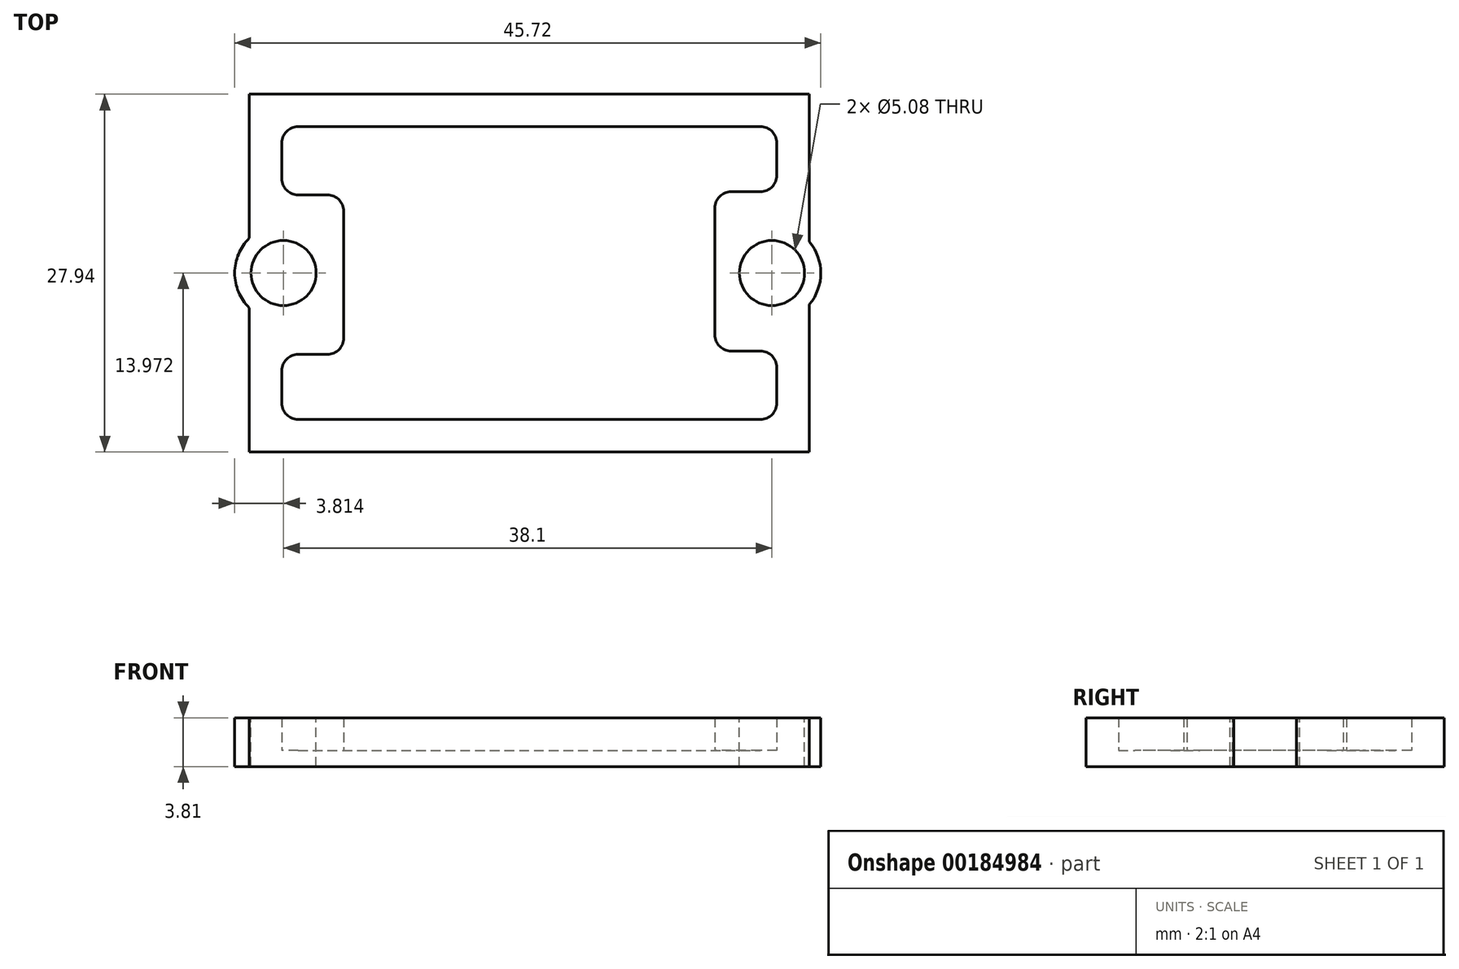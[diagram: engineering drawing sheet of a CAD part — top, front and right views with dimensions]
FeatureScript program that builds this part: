
annotation { "Feature Type Name" : "Feature", "Feature Type Description" : "" }
export const myFeature = defineFeature(function(context is Context, id is Id, definition is map)
    precondition{}
    {
        {
            var Q0;
            Q0=qCreatedBy(makeId("Top.planeOp"),FACE);
            var sketch = newSketch(context, id + "F0", { "sketchPlane" : qUnion([Q0])});
            skLineSegment(sketch, "E0.bottom", {"start": v(-19.02, 13.8) * mm, "end": v(17.05, 13.8) * mm});
            skLineSegment(sketch, "E0.top", {"start": v(-19.02, -9.06) * mm, "end": v(17.05, -9.06) * mm});
            skLineSegment(sketch, "E0.left", {"start": v(-20.3, -5.25) * mm, "end": v(-20.3, -7.79) * mm});
            skLineSegment(sketch, "E0.right", {"start": v(18.32, 12.53) * mm, "end": v(18.32, 10) * mm});
            skLineSegment(sketch, "E1.bottom", {"start": v(-19.02, 8.47) * mm, "end": v(-16.74, 8.47) * mm});
            skLineSegment(sketch, "E1.top", {"start": v(-19.02, -3.98) * mm, "end": v(-16.74, -3.98) * mm});
            skLineSegment(sketch, "E1.right", {"start": v(-15.47, 7.2) * mm, "end": v(-15.47, -2.7) * mm});
            skLineSegment(sketch, "E2.bottom", {"start": v(17.05, 8.72) * mm, "end": v(14.76, 8.72) * mm});
            skLineSegment(sketch, "E2.top", {"start": v(17.05, -3.72) * mm, "end": v(14.76, -3.72) * mm});
            skLineSegment(sketch, "E2.right", {"start": v(13.49, 7.45) * mm, "end": v(13.49, -2.45) * mm});
            skPoint(sketch, "E3.visualSharp", {"position": v(-15.47, 8.47) * mm});
            skArc(sketch, "E3.filletArc", {"start": v(-15.47, 7.2) * mm, "mid": v(-15.84, 8.1) * mm, "end": v(-16.74, 8.47) * mm});
            skPoint(sketch, "E4.visualSharp", {"position": v(-15.47, -3.98) * mm});
            skArc(sketch, "E4.filletArc", {"start": v(-16.74, -3.98) * mm, "mid": v(-15.84, -3.6) * mm, "end": v(-15.47, -2.7) * mm});
            skArc(sketch, "E5.filletArc", {"start": v(-19.02, -3.98) * mm, "mid": v(-19.92, -4.35) * mm, "end": v(-20.3, -5.25) * mm});
            skPoint(sketch, "E6.visualSharp", {"position": v(-20.3, -9.06) * mm});
            skArc(sketch, "E6.filletArc", {"start": v(-20.3, -7.79) * mm, "mid": v(-19.92, -8.69) * mm, "end": v(-19.02, -9.06) * mm});
            skLineSegment(sketch, "E7", {"start": v(-20.3, 9.74) * mm, "end": v(-20.3, 12.53) * mm});
            skPoint(sketch, "E8.visualSharp", {"position": v(-20.3, 13.8) * mm});
            skArc(sketch, "E8.filletArc", {"start": v(-19.02, 13.8) * mm, "mid": v(-19.92, 13.43) * mm, "end": v(-20.3, 12.53) * mm});
            skPoint(sketch, "E9.visualSharp", {"position": v(-20.3, 8.47) * mm});
            skArc(sketch, "E9.filletArc", {"start": v(-20.3, 9.74) * mm, "mid": v(-19.92, 8.84) * mm, "end": v(-19.02, 8.47) * mm});
            skPoint(sketch, "E10.newPointA", {"position": v(18.32, 8.72) * mm});
            skPoint(sketch, "E10.newPointB", {"position": v(18.32, -9.06) * mm});
            skArc(sketch, "E10.filletArc", {"start": v(17.05, 8.72) * mm, "mid": v(17.94, 9.1) * mm, "end": v(18.32, 10) * mm});
            skLineSegment(sketch, "E11", {"start": v(18.32, -5) * mm, "end": v(18.32, -7.79) * mm});
            skPoint(sketch, "E12.visualSharp", {"position": v(13.49, 8.72) * mm});
            skArc(sketch, "E12.filletArc", {"start": v(14.76, 8.72) * mm, "mid": v(13.86, 8.35) * mm, "end": v(13.49, 7.45) * mm});
            skPoint(sketch, "E13.visualSharp", {"position": v(18.32, -3.72) * mm});
            skArc(sketch, "E13.filletArc", {"start": v(18.32, -5) * mm, "mid": v(17.94, -4.1) * mm, "end": v(17.05, -3.72) * mm});
            skPoint(sketch, "E14.visualSharp", {"position": v(13.49, -3.72) * mm});
            skArc(sketch, "E14.filletArc", {"start": v(13.49, -2.45) * mm, "mid": v(13.86, -3.35) * mm, "end": v(14.76, -3.72) * mm});
            skPoint(sketch, "E15.visualSharp", {"position": v(18.32, 13.8) * mm});
            skArc(sketch, "E15.filletArc", {"start": v(18.32, 12.53) * mm, "mid": v(17.94, 13.43) * mm, "end": v(17.05, 13.8) * mm});
            skArc(sketch, "E16.filletArc", {"start": v(17.05, -9.06) * mm, "mid": v(17.94, -8.69) * mm, "end": v(18.32, -7.79) * mm});
            skLineSegment(sketch, "E17.bottom", {"start": v(-22.83, 16.34) * mm, "end": v(20.86, 16.34) * mm});
            skLineSegment(sketch, "E17.top", {"start": v(-22.83, -11.6) * mm, "end": v(20.86, -11.6) * mm});
            skLineSegment(sketch, "E17.left", {"start": v(-22.83, 16.34) * mm, "end": v(-22.83, -11.6) * mm});
            skLineSegment(sketch, "E17.right", {"start": v(20.86, 16.34) * mm, "end": v(20.86, -11.6) * mm});
            skSolve(sketch);
        }
        {
            var Q0;
            Q0=makeQuery(id+"F0.imprint","IMPRINT",FACE,{"disambiguationData":[TD([[makeQuery(id+"F0.imprint","IMPRINT",EDGE,{"derivedFrom":sQuery(id+"F0.wireOp",EDGE,"E0.bottom")}),1.0]])]});
            extrude(context, id + "F1", {"entities" : qUnion([Q0]), "depth" : 3.8 * mm});
        }
        {
            var Q0;
            Q0=makeQuery(id+"F0.imprint","IMPRINT",FACE,{"disambiguationData":[TD([[makeQuery(id+"F0.imprint","IMPRINT",EDGE,{"derivedFrom":sQuery(id+"F0.wireOp",EDGE,"E0.bottom")}),-1.0]])]});
            extrude(context, id + "F2", {"entities" : qUnion([Q0]), "operationType" : NewBodyOperationType.ADD, "depth" : 1.27 * mm});
        }
        {
            var Q0;
            Q0=makeQuery(id+"F1.opExtrude","CAP_FACE",FACE,{"disambiguationData":[OSD([sQuery(id+"F0.wireOp",EDGE,"E0.bottom"),sQuery(id+"F0.wireOp",EDGE,"E0.top"),sQuery(id+"F0.wireOp",EDGE,"E0.left"),sQuery(id+"F0.wireOp",EDGE,"E0.right"),sQuery(id+"F0.wireOp",EDGE,"E1.bottom"),sQuery(id+"F0.wireOp",EDGE,"E1.top"),sQuery(id+"F0.wireOp",EDGE,"E1.right"),sQuery(id+"F0.wireOp",EDGE,"E2.bottom"),sQuery(id+"F0.wireOp",EDGE,"E2.top"),sQuery(id+"F0.wireOp",EDGE,"E2.right"),sQuery(id+"F0.wireOp",EDGE,"E3.filletArc"),sQuery(id+"F0.wireOp",EDGE,"E4.filletArc"),sQuery(id+"F0.wireOp",EDGE,"E5.filletArc"),sQuery(id+"F0.wireOp",EDGE,"E6.filletArc"),sQuery(id+"F0.wireOp",EDGE,"E7"),sQuery(id+"F0.wireOp",EDGE,"E8.filletArc"),sQuery(id+"F0.wireOp",EDGE,"E9.filletArc"),sQuery(id+"F0.wireOp",EDGE,"E10.filletArc"),sQuery(id+"F0.wireOp",EDGE,"E11"),sQuery(id+"F0.wireOp",EDGE,"E12.filletArc"),sQuery(id+"F0.wireOp",EDGE,"E13.filletArc"),sQuery(id+"F0.wireOp",EDGE,"E14.filletArc"),sQuery(id+"F0.wireOp",EDGE,"E15.filletArc"),sQuery(id+"F0.wireOp",EDGE,"E16.filletArc"),sQuery(id+"F0.wireOp",EDGE,"E17.bottom"),sQuery(id+"F0.wireOp",EDGE,"E17.top"),sQuery(id+"F0.wireOp",EDGE,"E17.left"),sQuery(id+"F0.wireOp",EDGE,"E17.right")])],"isStart":false});
            var sketch = newSketch(context, id + "F3", { "sketchPlane" : qUnion([Q0])});
            skCircle(sketch, "E18", {"center": v(-20.17, 2.37) * mm, "radius": 3.81 * mm});
            skCircle(sketch, "E19", {"center": v(17.93, 2.37) * mm, "radius": 3.81 * mm});
            skCircle(sketch, "E20", {"center": v(-20.17, 2.37) * mm, "radius": 2.54 * mm});
            skCircle(sketch, "E21", {"center": v(17.93, 2.37) * mm, "radius": 2.54 * mm});
            skSolve(sketch);
        }
        {
            var Q0;
            {var subQ0=sQuery(id+"F3.wireOp",EDGE,"E18");var subQ1=makeQuery(id+"F1.opExtrude","CAP_EDGE",EDGE,{"disambiguationData":[OSD([sQuery(id+"F0.wireOp",EDGE,"E17.left")])],"isStart":false});var subQ2=makeQuery(id+"F3.imprint","INTERSECT",VERTEX,{"disambiguationData":[OD(0.0)],"derivedFrom":[subQ1,subQ0]});Q0=makeQuery(id+"F3.imprint","IMPRINT",FACE,{"disambiguationData":[TD([[makeQuery(id+"F3.imprint","IMPRINT",EDGE,{"disambiguationData":[TD([[subQ2,-1.0]])],"derivedFrom":subQ0}),1.0]])]});}
            var Q1;
            {var subQ0=sQuery(id+"F3.wireOp",EDGE,"E19");var subQ1=makeQuery(id+"F1.opExtrude","CAP_EDGE",EDGE,{"disambiguationData":[OSD([sQuery(id+"F0.wireOp",EDGE,"E17.right")])],"isStart":false});var subQ2=makeQuery(id+"F3.imprint","INTERSECT",VERTEX,{"disambiguationData":[OD(0.0)],"derivedFrom":[subQ1,subQ0]});Q1=makeQuery(id+"F3.imprint","IMPRINT",FACE,{"disambiguationData":[TD([[makeQuery(id+"F3.imprint","IMPRINT",EDGE,{"disambiguationData":[TD([[subQ2,1.0]])],"derivedFrom":subQ0}),1.0]])]});}
            extrude(context, id + "F4", {"entities" : qUnion([Q0, Q1]), "operationType" : NewBodyOperationType.ADD, "oppositeDirection" : true, "depth" : 3.8 * mm});
        }
        {
            var Q0;
            Q0=makeQuery(id+"F3.imprint","IMPRINT",FACE,{"disambiguationData":[TD([[makeQuery(id+"F3.imprint","IMPRINT",EDGE,{"derivedFrom":sQuery(id+"F3.wireOp",EDGE,"E20")}),1.0]])]});
            var Q1;
            Q1=makeQuery(id+"F3.imprint","IMPRINT",FACE,{"disambiguationData":[TD([[makeQuery(id+"F3.imprint","IMPRINT",EDGE,{"derivedFrom":sQuery(id+"F3.wireOp",EDGE,"E21")}),1.0]])]});
            extrude(context, id + "F5", {"entities" : qUnion([Q0, Q1]), "operationType" : NewBodyOperationType.REMOVE, "oppositeDirection" : true, "depth" : 25.4 * mm});
        }
    });
